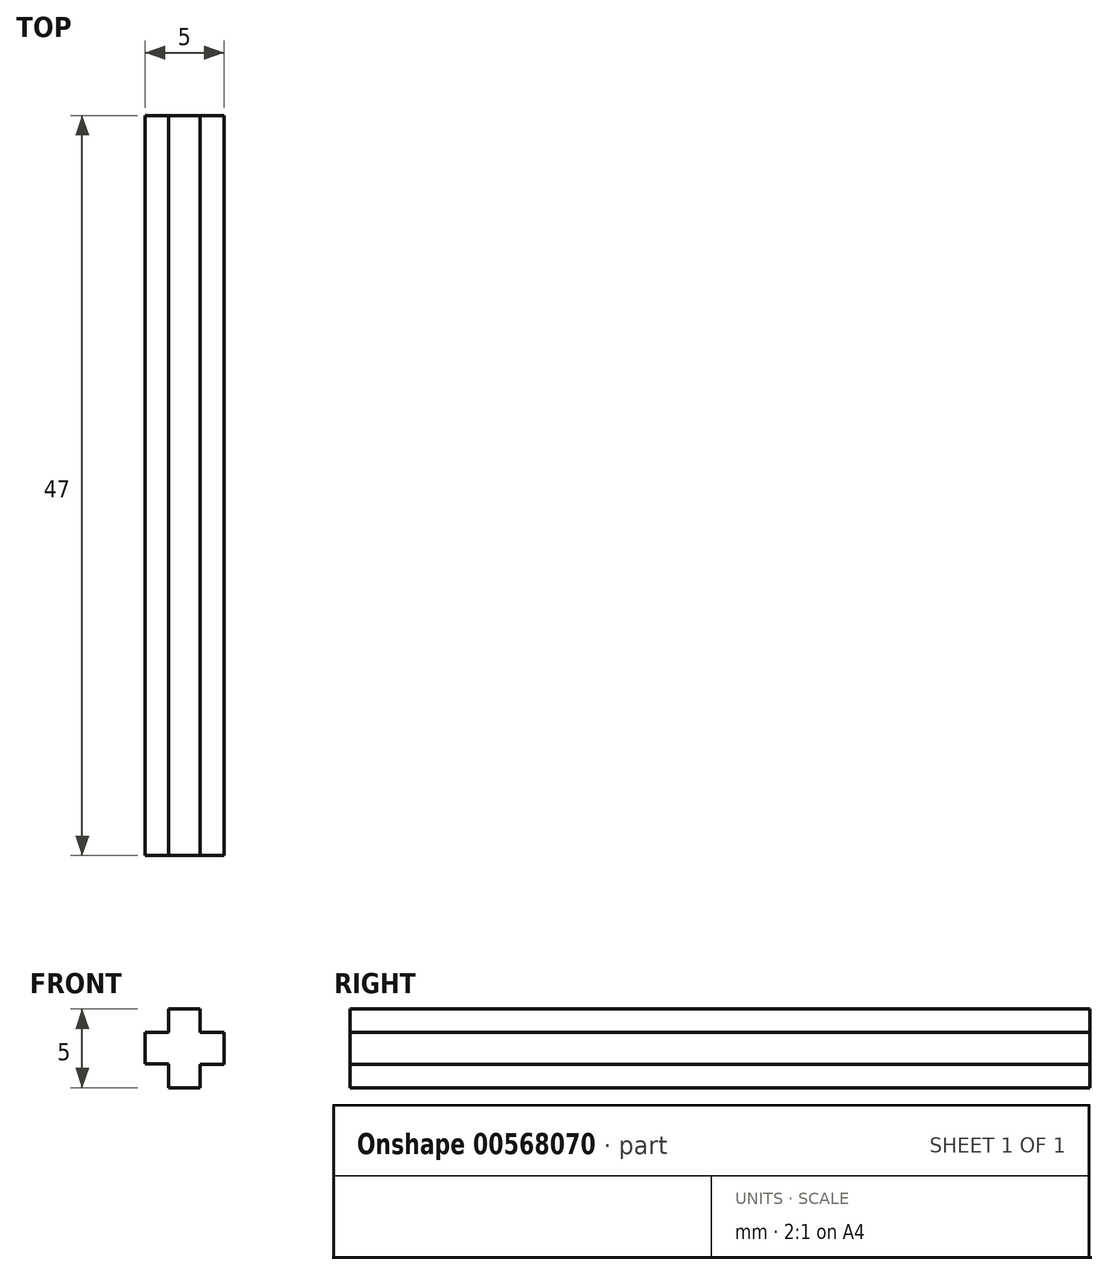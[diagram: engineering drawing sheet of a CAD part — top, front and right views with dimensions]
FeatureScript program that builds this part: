
annotation { "Feature Type Name" : "Feature", "Feature Type Description" : "" }
export const myFeature = defineFeature(function(context is Context, id is Id, definition is map)
    precondition{}
    {
        {
            var Q0;
            Q0=qCreatedBy(makeId("Front.planeOp"),FACE);
            var sketch = newSketch(context, id + "F0", { "sketchPlane" : qUnion([Q0])});
            skLineSegment(sketch, "E0", {"start": v(0.04, -2.5) * mm, "end": v(1.04, -2.5) * mm});
            skLineSegment(sketch, "E1", {"start": v(0.04, -2.5) * mm, "end": v(-0.96, -2.5) * mm});
            skLineSegment(sketch, "E2", {"start": v(-0.96, -2.5) * mm, "end": v(-0.96, -1) * mm});
            skLineSegment(sketch, "E3", {"start": v(1.04, -2.5) * mm, "end": v(1.04, -1) * mm});
            skLineSegment(sketch, "E4", {"start": v(-0.96, -1) * mm, "end": v(-2.46, -1) * mm});
            skLineSegment(sketch, "E5", {"start": v(1.04, -1) * mm, "end": v(2.54, -1) * mm});
            skLineSegment(sketch, "E6", {"start": v(-2.46, -1) * mm, "end": v(-2.46, 1) * mm});
            skLineSegment(sketch, "E7", {"start": v(2.54, -1) * mm, "end": v(2.54, 1) * mm});
            skLineSegment(sketch, "E8", {"start": v(2.54, 1) * mm, "end": v(1.04, 1) * mm});
            skLineSegment(sketch, "E9", {"start": v(-2.46, 1) * mm, "end": v(-0.96, 1) * mm});
            skLineSegment(sketch, "E10", {"start": v(-0.96, 1) * mm, "end": v(-0.96, 2.5) * mm});
            skLineSegment(sketch, "E11", {"start": v(1.04, 1) * mm, "end": v(1.04, 2.5) * mm});
            skLineSegment(sketch, "E12", {"start": v(-0.96, 2.5) * mm, "end": v(1.04, 2.5) * mm});
            skSolve(sketch);
        }
        {
            var Q0;
            Q0=makeQuery(id+"F0.imprint","IMPRINT",FACE,{"disambiguationData":[TD([[makeQuery(id+"F0.imprint","IMPRINT",EDGE,{"derivedFrom":sQuery(id+"F0.wireOp",EDGE,"E0")}),1.0]])]});
            extrude(context, id + "F1", {"entities" : qUnion([Q0]), "depth" : 47 * mm, "offsetDistance" : 25.4 * mm});
        }
    });
